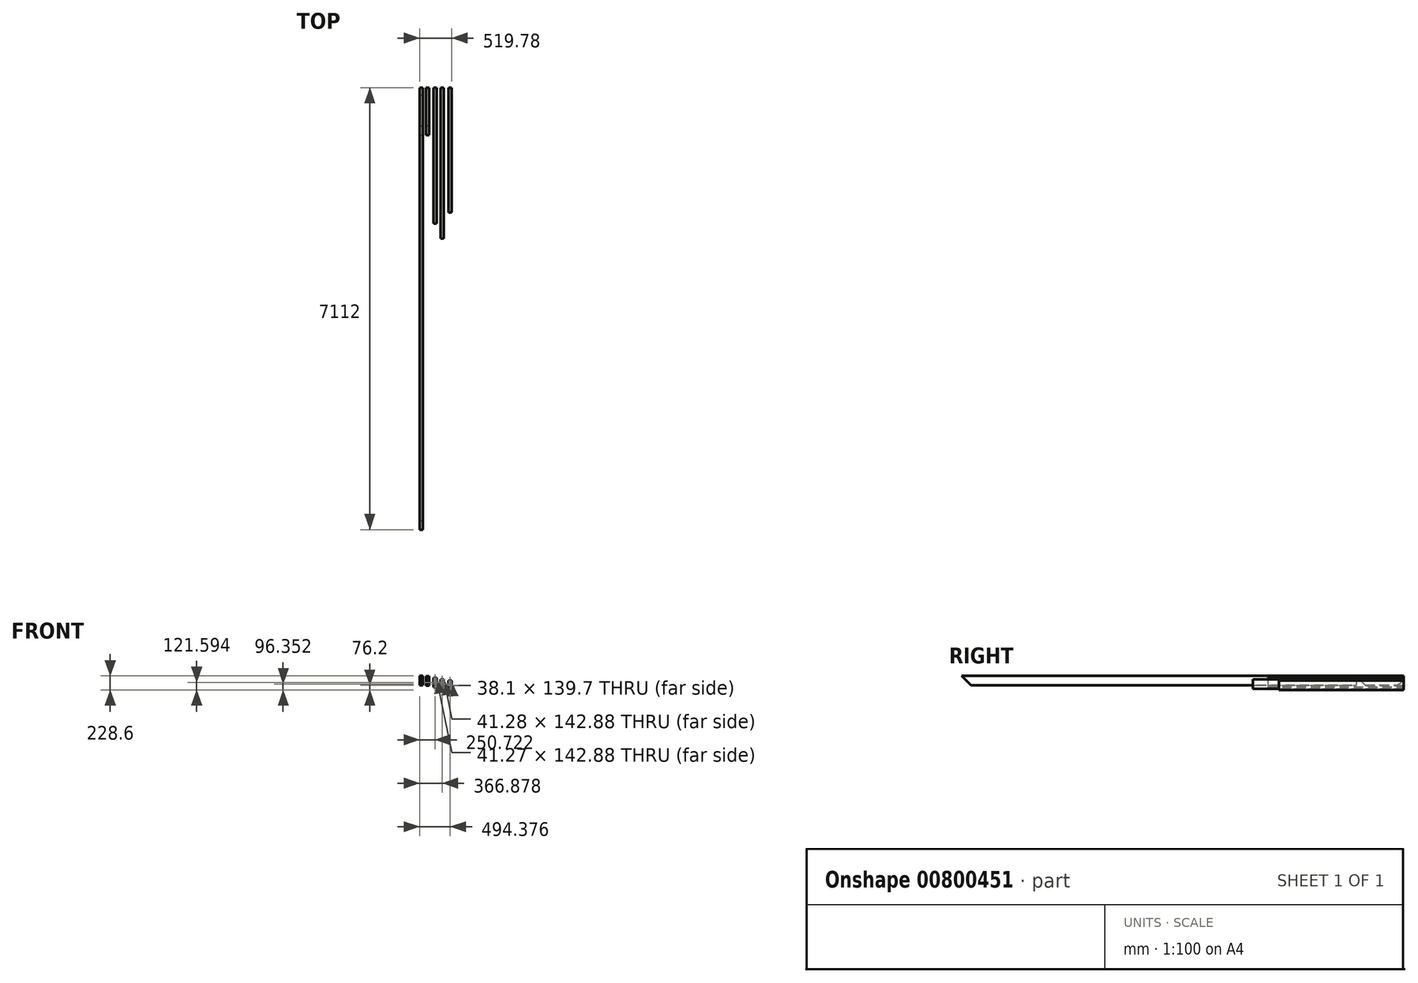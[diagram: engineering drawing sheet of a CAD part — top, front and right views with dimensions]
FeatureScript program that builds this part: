
annotation { "Feature Type Name" : "Feature", "Feature Type Description" : "" }
export const myFeature = defineFeature(function(context is Context, id is Id, definition is map)
    precondition{}
    {
        {
            var Q0;
            Q0=qCreatedBy(makeId("Front.planeOp"),FACE);
            var sketch = newSketch(context, id + "F0", { "sketchPlane" : qUnion([Q0])});
            skLineSegment(sketch, "E0.bottom", {"start": v(-25.4, 76.2) * mm, "end": v(25.4, 76.2) * mm});
            skLineSegment(sketch, "E0.top", {"start": v(-25.4, -76.2) * mm, "end": v(25.4, -76.2) * mm});
            skLineSegment(sketch, "E0.left", {"start": v(-25.4, 76.2) * mm, "end": v(-25.4, -76.2) * mm});
            skLineSegment(sketch, "E0.right", {"start": v(25.4, 76.2) * mm, "end": v(25.4, -76.2) * mm});
            skPoint(sketch, "E0.middle", {"position": v(0, 0) * mm});
            skLineSegment(sketch, "E1.0", {"start": v(-20.64, 71.44) * mm, "end": v(20.64, 71.44) * mm});
            skLineSegment(sketch, "E1.1", {"start": v(-20.64, 71.44) * mm, "end": v(-20.64, -71.44) * mm});
            skLineSegment(sketch, "E1.2", {"start": v(-20.64, -71.44) * mm, "end": v(20.64, -71.44) * mm});
            skLineSegment(sketch, "E1.3", {"start": v(20.64, 71.44) * mm, "end": v(20.64, -71.44) * mm});
            skSolve(sketch);
        }
        {
            var Q0;
            Q0=makeQuery(id+"F0.imprint","IMPRINT",FACE,{"disambiguationData":[TD([[makeQuery(id+"F0.imprint","IMPRINT",EDGE,{"derivedFrom":sQuery(id+"F0.wireOp",EDGE,"E0.bottom")}),-1.0]])]});
            extrude(context, id + "F1", {"entities" : qUnion([Q0]), "depth" : 7112 * mm, "offsetDistance" : 25.4 * mm});
        }
        {
            var Q0;
            Q0=makeQuery(id+"F1.opExtrude","SWEPT_FACE",FACE,{"disambiguationData":[OSD([sQuery(id+"F0.wireOp",EDGE,"E0.bottom")])]});
            var sketch = newSketch(context, id + "F2", { "sketchPlane" : qUnion([Q0])});
            skLineSegment(sketch, "E2.bottom", {"start": v(-25.4, 210.64) * mm, "end": v(25.4, 210.64) * mm});
            skLineSegment(sketch, "E2.top", {"start": v(-25.4, 0) * mm, "end": v(25.4, 0) * mm});
            skLineSegment(sketch, "E2.left", {"start": v(-25.4, 210.64) * mm, "end": v(-25.4, 0) * mm});
            skLineSegment(sketch, "E2.right", {"start": v(25.4, 210.64) * mm, "end": v(25.4, 0) * mm});
            skLineSegment(sketch, "E3", {"start": v(-25.4, -152.4) * mm, "end": v(25.4, -152.4) * mm, "construction": true});
            skSolve(sketch);
        }
        {
            var Q0;
            Q0 = qSketchRegion(id + "F2", true);
            var Q1;
            Q1=sQuery(id+"F2.wireOp",EDGE,"E3");
            revolve(context, id + "F3", {"operationType" : NewBodyOperationType.REMOVE, "surfaceOperationType" : NewSurfaceOperationType.NEW, "entities" : qUnion([Q0]), "axis" : qUnion([Q1]), "revolveType" : RevolveType.ONE_DIRECTION, "oppositeDirection" : true, "angle" : 90 * degree});
        }
        {
            var Q0;
            Q0=makeQuery(id+"F1.opExtrude","SWEPT_FACE",FACE,{"disambiguationData":[OSD([sQuery(id+"F0.wireOp",EDGE,"E0.right")])]});
            var sketch = newSketch(context, id + "F4", { "sketchPlane" : qUnion([Q0])});
            skLineSegment(sketch, "E4", {"start": v(-7112, 76.2) * mm, "end": v(-6959.6, -76.2) * mm});
            skLineSegment(sketch, "E5", {"start": v(-6959.6, -76.2) * mm, "end": v(-7112, -76.2) * mm});
            skLineSegment(sketch, "E6", {"start": v(-7112, -76.2) * mm, "end": v(-7112, 76.2) * mm});
            skSolve(sketch);
        }
        {
            var Q0;
            Q0 = qSketchRegion(id + "F4", true);
            extrude(context, id + "F5", {"entities" : qUnion([Q0]), "operationType" : NewBodyOperationType.REMOVE, "endBound" : BoundingType.THROUGH_ALL, "oppositeDirection" : true, "depth" : 25.4 * mm, "offsetDistance" : 25.4 * mm});
        }
        {
            var Q0;
            Q0=qCreatedBy(makeId("Front.planeOp"),FACE);
            var sketch = newSketch(context, id + "F6", { "sketchPlane" : qUnion([Q0])});
            skLineSegment(sketch, "E7.bottom", {"start": v(79.3, 66.3) * mm, "end": v(130.1, 66.3) * mm});
            skLineSegment(sketch, "E7.top", {"start": v(79.3, -86.1) * mm, "end": v(130.1, -86.1) * mm});
            skLineSegment(sketch, "E7.left", {"start": v(79.3, 66.3) * mm, "end": v(79.3, -86.1) * mm});
            skLineSegment(sketch, "E7.right", {"start": v(130.1, 66.3) * mm, "end": v(130.1, -86.1) * mm});
            skPoint(sketch, "E7.middle", {"position": v(104.7, -9.9) * mm});
            skLineSegment(sketch, "E8.0", {"start": v(85.65, 59.96) * mm, "end": v(123.75, 59.96) * mm});
            skLineSegment(sketch, "E8.1", {"start": v(85.65, 59.96) * mm, "end": v(85.65, -79.74) * mm});
            skLineSegment(sketch, "E8.2", {"start": v(85.65, -79.74) * mm, "end": v(123.75, -79.74) * mm});
            skLineSegment(sketch, "E8.3", {"start": v(123.75, 59.96) * mm, "end": v(123.75, -79.74) * mm});
            skSolve(sketch);
        }
        {
            var Q0;
            Q0=makeQuery(id+"F6.imprint","IMPRINT",FACE,{"disambiguationData":[TD([[makeQuery(id+"F6.imprint","IMPRINT",EDGE,{"derivedFrom":sQuery(id+"F6.wireOp",EDGE,"E7.bottom")}),-1.0]])]});
            extrude(context, id + "F7", {"entities" : qUnion([Q0]), "depth" : 762 * mm, "offsetDistance" : 25.4 * mm});
        }
        {
            var Q0;
            Q0=makeQuery(id+"F7.opExtrude","SWEPT_FACE",FACE,{"disambiguationData":[OSD([sQuery(id+"F6.wireOp",EDGE,"E7.right")])]});
            var sketch = newSketch(context, id + "F8", { "sketchPlane" : qUnion([Q0])});
            skLineSegment(sketch, "E9", {"start": v(-762, 66.3) * mm, "end": v(-762, -86.1) * mm});
            skLineSegment(sketch, "E10", {"start": v(-762, -86.1) * mm, "end": v(-609.6, -86.1) * mm});
            skLineSegment(sketch, "E11", {"start": v(-609.6, -86.1) * mm, "end": v(-762, 66.3) * mm});
            skSolve(sketch);
        }
        {
            var Q0;
            Q0 = qSketchRegion(id + "F8", true);
            extrude(context, id + "F9", {"entities" : qUnion([Q0]), "operationType" : NewBodyOperationType.REMOVE, "endBound" : BoundingType.THROUGH_ALL, "oppositeDirection" : true, "depth" : 25.4 * mm, "offsetDistance" : 25.4 * mm});
        }
        {
            var Q0;
            Q0=qCreatedBy(makeId("Front.planeOp"),FACE);
            var sketch = newSketch(context, id + "F10", { "sketchPlane" : qUnion([Q0])});
            skLineSegment(sketch, "E12.bottom", {"start": v(199.92, 45.4) * mm, "end": v(250.72, 45.4) * mm});
            skLineSegment(sketch, "E12.top", {"start": v(199.92, -107) * mm, "end": v(250.72, -107) * mm});
            skLineSegment(sketch, "E12.left", {"start": v(199.92, 45.4) * mm, "end": v(199.92, -107) * mm});
            skLineSegment(sketch, "E12.right", {"start": v(250.72, 45.4) * mm, "end": v(250.72, -107) * mm});
            skLineSegment(sketch, "E13.0", {"start": v(204.68, 40.63) * mm, "end": v(245.96, 40.63) * mm});
            skLineSegment(sketch, "E13.1", {"start": v(204.68, 40.63) * mm, "end": v(204.68, -102.24) * mm});
            skLineSegment(sketch, "E13.2", {"start": v(204.68, -102.24) * mm, "end": v(245.96, -102.24) * mm});
            skLineSegment(sketch, "E13.3", {"start": v(245.96, 40.63) * mm, "end": v(245.96, -102.24) * mm});
            skSolve(sketch);
        }
        {
            var Q0;
            Q0=makeQuery(id+"F10.imprint","IMPRINT",FACE,{"disambiguationData":[TD([[makeQuery(id+"F10.imprint","IMPRINT",EDGE,{"derivedFrom":sQuery(id+"F10.wireOp",EDGE,"E12.bottom")}),-1.0]])]});
            extrude(context, id + "F11", {"entities" : qUnion([Q0]), "depth" : 2184.4 * mm, "offsetDistance" : 25.4 * mm});
        }
        {
            var Q0;
            Q0=qCreatedBy(makeId("Front.planeOp"),FACE);
            var sketch = newSketch(context, id + "F12", { "sketchPlane" : qUnion([Q0])});
            skLineSegment(sketch, "E14.bottom", {"start": v(316.08, 20.15) * mm, "end": v(366.88, 20.15) * mm});
            skLineSegment(sketch, "E14.top", {"start": v(316.08, -132.25) * mm, "end": v(366.88, -132.25) * mm});
            skLineSegment(sketch, "E14.left", {"start": v(316.08, 20.15) * mm, "end": v(316.08, -132.25) * mm});
            skLineSegment(sketch, "E14.right", {"start": v(366.88, 20.15) * mm, "end": v(366.88, -132.25) * mm});
            skLineSegment(sketch, "E15.0", {"start": v(320.84, 15.39) * mm, "end": v(362.12, 15.39) * mm});
            skLineSegment(sketch, "E15.1", {"start": v(320.84, 15.39) * mm, "end": v(320.84, -127.49) * mm});
            skLineSegment(sketch, "E15.2", {"start": v(320.84, -127.49) * mm, "end": v(362.12, -127.49) * mm});
            skLineSegment(sketch, "E15.3", {"start": v(362.12, 15.39) * mm, "end": v(362.12, -127.49) * mm});
            skSolve(sketch);
        }
        {
            var Q0;
            Q0=makeQuery(id+"F12.imprint","IMPRINT",FACE,{"disambiguationData":[TD([[makeQuery(id+"F12.imprint","IMPRINT",EDGE,{"derivedFrom":sQuery(id+"F12.wireOp",EDGE,"E14.bottom")}),-1.0]])]});
            extrude(context, id + "F13", {"entities" : qUnion([Q0]), "depth" : 2425.7 * mm, "offsetDistance" : 25.4 * mm});
        }
        {
            var Q0;
            Q0=qCreatedBy(makeId("Front.planeOp"),FACE);
            var sketch = newSketch(context, id + "F14", { "sketchPlane" : qUnion([Q0])});
            skLineSegment(sketch, "E16.bottom", {"start": v(443.58, 0) * mm, "end": v(494.38, 0) * mm});
            skLineSegment(sketch, "E16.top", {"start": v(443.58, -152.4) * mm, "end": v(494.38, -152.4) * mm});
            skLineSegment(sketch, "E16.left", {"start": v(443.58, 0) * mm, "end": v(443.58, -152.4) * mm});
            skLineSegment(sketch, "E16.right", {"start": v(494.38, 0) * mm, "end": v(494.38, -152.4) * mm});
            skLineSegment(sketch, "E17.0", {"start": v(449.93, -6.35) * mm, "end": v(488.03, -6.35) * mm});
            skLineSegment(sketch, "E17.1", {"start": v(449.93, -6.35) * mm, "end": v(449.93, -146.05) * mm});
            skLineSegment(sketch, "E17.2", {"start": v(449.93, -146.05) * mm, "end": v(488.03, -146.05) * mm});
            skLineSegment(sketch, "E17.3", {"start": v(488.03, -6.35) * mm, "end": v(488.03, -146.05) * mm});
            skSolve(sketch);
        }
        {
            var Q0;
            Q0=makeQuery(id+"F14.imprint","IMPRINT",FACE,{"disambiguationData":[TD([[makeQuery(id+"F14.imprint","IMPRINT",EDGE,{"derivedFrom":sQuery(id+"F14.wireOp",EDGE,"E16.bottom")}),-1.0]])]});
            extrude(context, id + "F15", {"entities" : qUnion([Q0]), "depth" : 2006.6 * mm, "offsetDistance" : 25.4 * mm});
        }
    });
